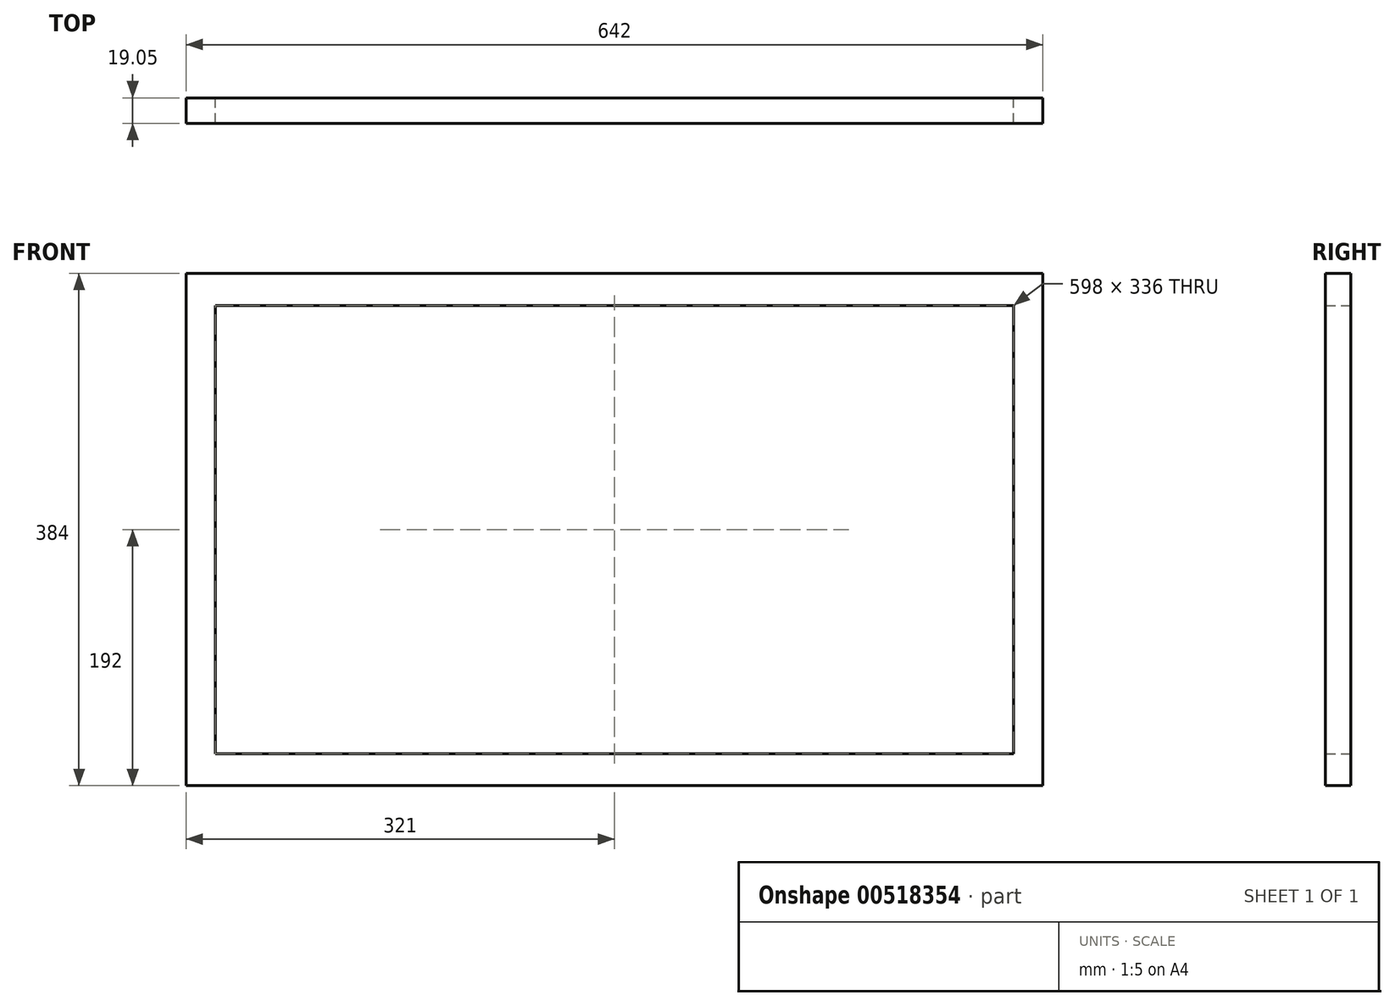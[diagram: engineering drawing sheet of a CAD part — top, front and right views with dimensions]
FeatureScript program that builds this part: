
annotation { "Feature Type Name" : "Feature", "Feature Type Description" : "" }
export const myFeature = defineFeature(function(context is Context, id is Id, definition is map)
    precondition{}
    {
        {
            var Q0;
            Q0=qCreatedBy(makeId("Front.planeOp"),FACE);
            var sketch = newSketch(context, id + "F0", { "sketchPlane" : qUnion([Q0])});
            skLineSegment(sketch, "E0.bottom", {"start": v(-321, 192) * mm, "end": v(321, 192) * mm});
            skLineSegment(sketch, "E0.top", {"start": v(-321, -192) * mm, "end": v(321, -192) * mm});
            skLineSegment(sketch, "E0.left", {"start": v(-321, 192) * mm, "end": v(-321, -192) * mm});
            skLineSegment(sketch, "E0.right", {"start": v(321, 192) * mm, "end": v(321, -192) * mm});
            skPoint(sketch, "E0.middle", {"position": v(0, 0) * mm});
            skSolve(sketch);
        }
        {
            var Q0;
            Q0=makeQuery(id+"F0.imprint","IMPRINT",FACE,{"disambiguationData":[TD([[makeQuery(id+"F0.imprint","IMPRINT",EDGE,{"derivedFrom":sQuery(id+"F0.wireOp",EDGE,"E0.bottom")}),-1.0]])]});
            extrude(context, id + "F1", {"entities" : qUnion([Q0]), "depth" : 19.05 * mm});
        }
        {
            var Q0;
            Q0=qCreatedBy(makeId("Front.planeOp"),FACE);
            var sketch = newSketch(context, id + "F2", { "sketchPlane" : qUnion([Q0])});
            skLineSegment(sketch, "E1.bottom", {"start": v(-299, 168) * mm, "end": v(299, 168) * mm});
            skLineSegment(sketch, "E1.top", {"start": v(-299, -168) * mm, "end": v(299, -168) * mm});
            skLineSegment(sketch, "E1.left", {"start": v(-299, 168) * mm, "end": v(-299, -168) * mm});
            skLineSegment(sketch, "E1.right", {"start": v(299, 168) * mm, "end": v(299, -168) * mm});
            skPoint(sketch, "E1.middle", {"position": v(0, 0) * mm});
            skSolve(sketch);
        }
        {
            var Q0;
            Q0=qSketchRegion(id+"F2",true);
            extrude(context, id + "F3", {"entities" : qUnion([Q0]), "operationType" : NewBodyOperationType.REMOVE, "depth" : 365.76 * mm});
        }
    });
